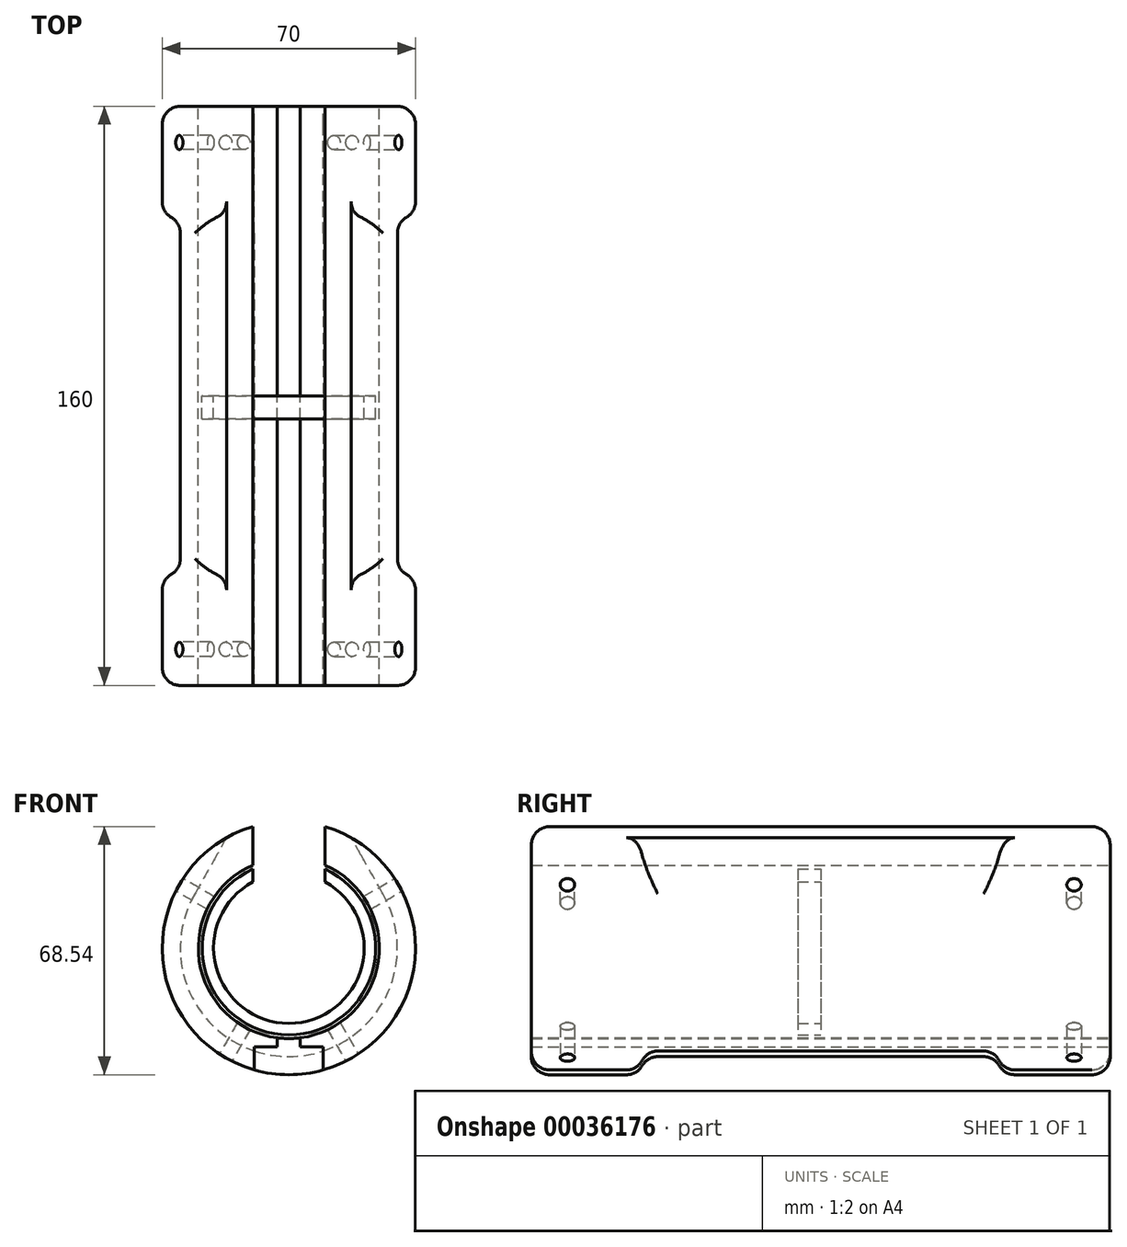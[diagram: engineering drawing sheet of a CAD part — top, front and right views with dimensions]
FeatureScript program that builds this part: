
annotation { "Feature Type Name" : "Feature", "Feature Type Description" : "" }
export const myFeature = defineFeature(function(context is Context, id is Id, definition is map)
    precondition{}
    {
        {
            assignVariable(context, id + "F0", {"name" : "Len", "anyValue" : 160 * mm});
        }
        {
            assignVariable(context, id + "F1", {"name" : "ScrewDia", "anyValue" : 4 * mm});
        }
        {
            assignVariable(context, id + "F2", {"name" : "FilletRadius", "anyValue" : 5 * mm});
        }
        {
            var Q0;
            Q0=qCreatedBy(makeId("Front.planeOp"),FACE);
            var sketch = newSketch(context, id + "F3", { "sketchPlane" : qUnion([Q0])});
            skArc(sketch, "E0", {"start": v(-10, 22.91) * mm, "mid": v(0, -25) * mm, "end": v(10, 22.91) * mm});
            skArc(sketch, "E1", {"start": v(-10, 33.54) * mm, "mid": v(0, -35) * mm, "end": v(10, 33.54) * mm});
            skPoint(sketch, "E2.orphan", {"position": v(-10, 33.54) * mm});
            skLineSegment(sketch, "E3", {"start": v(-10, 33.54) * mm, "end": v(-10, 22.91) * mm});
            skLineSegment(sketch, "E4", {"start": v(10, 33.54) * mm, "end": v(10, 22.91) * mm});
            skLineSegment(sketch, "E5", {"start": v(-17.5, -30.31) * mm, "end": v(17.5, -30.31) * mm, "construction": true});
            skLineSegment(sketch, "E6", {"start": v(17.5, -30.31) * mm, "end": v(30.31, 17.5) * mm, "construction": true});
            skLineSegment(sketch, "E7.MirrorCS", {"start": v(-17.5, -30.31) * mm, "end": v(-30.31, 17.5) * mm, "construction": true});
            skLineSegment(sketch, "E8", {"start": v(30.31, 17.5) * mm, "end": v(0, 0) * mm, "construction": true});
            skLineSegment(sketch, "E9", {"start": v(0, 0) * mm, "end": v(17.5, -30.31) * mm, "construction": true});
            skLineSegment(sketch, "E10", {"start": v(0, 0) * mm, "end": v(-17.5, -30.31) * mm, "construction": true});
            skLineSegment(sketch, "E11", {"start": v(0, 0) * mm, "end": v(-30.31, 17.5) * mm, "construction": true});
            skArc(sketch, "E12", {"start": v(-25.98, 15) * mm, "mid": v(0, -30) * mm, "end": v(25.98, 15) * mm});
            skLineSegment(sketch, "E13", {"start": v(-17.23, 30.46) * mm, "end": v(-25.98, 15) * mm});
            skLineSegment(sketch, "E14", {"start": v(-10, 22.91) * mm, "end": v(-17.23, 30.46) * mm, "construction": true});
            skLineSegment(sketch, "E15.MirrorCS", {"start": v(17.23, 30.46) * mm, "end": v(25.98, 15) * mm});
            skLineSegment(sketch, "E16.MirrorCS", {"start": v(10, 22.91) * mm, "end": v(17.23, 30.46) * mm, "construction": true});
            skLineSegment(sketch, "E17.left", {"start": v(-3.17, -24.8) * mm, "end": v(-3.17, -27.33) * mm});
            skLineSegment(sketch, "E17.right", {"start": v(3.18, -24.8) * mm, "end": v(3.18, -27.33) * mm});
            skLineSegment(sketch, "E18.top", {"start": v(9.53, -27.33) * mm, "end": v(3.18, -27.33) * mm});
            skLineSegment(sketch, "E18.left", {"start": v(9.53, -33.68) * mm, "end": v(9.53, -27.33) * mm});
            skLineSegment(sketch, "E18.right", {"start": v(-9.52, -33.68) * mm, "end": v(-9.52, -27.33) * mm});
            skLineSegment(sketch, "E19.trimOffspring", {"start": v(-3.17, -27.33) * mm, "end": v(-9.52, -27.33) * mm});
            skLineSegment(sketch, "E20", {"start": v(0, 0) * mm, "end": v(0, -25) * mm, "construction": true});
            skLineSegment(sketch, "E21", {"start": v(-21.65, 12.5) * mm, "end": v(-20.77, 12) * mm, "construction": true});
            skCircle(sketch, "E22", {"center": v(0, 0) * mm, "radius": 23.98 * mm, "construction": true});
            skLineSegment(sketch, "E23", {"start": v(-20.77, 12) * mm, "end": v(-18.02, 10.4) * mm, "construction": true});
            skArc(sketch, "E24", {"start": v(-10, 21.8) * mm, "mid": v(0, -23.98) * mm, "end": v(10, 21.8) * mm});
            skArc(sketch, "E25", {"start": v(-10, 18.25) * mm, "mid": v(0, -20.8) * mm, "end": v(10, 18.25) * mm});
            skLineSegment(sketch, "E26", {"start": v(-10, 21.8) * mm, "end": v(-10, 18.25) * mm});
            skLineSegment(sketch, "E27", {"start": v(10, 21.8) * mm, "end": v(10, 18.25) * mm});
            skLineSegment(sketch, "E28", {"start": v(0, 0) * mm, "end": v(-17.23, 30.46) * mm, "construction": true});
            skLineSegment(sketch, "E29", {"start": v(0, 0) * mm, "end": v(17.23, 30.46) * mm, "construction": true});
            skSolve(sketch);
        }
        {
            var Q0;
            {var subQ6=sQuery(id+"F3.wireOp",EDGE,"E4");Q0=makeQuery(id+"F3.imprint","IMPRINT",FACE,{"disambiguationData":[TD([[makeQuery(id+"F3.imprint","IMPRINT",EDGE,{"derivedFrom":subQ6}),1.0]])]});}
            var Q1;
            {var subQ4=sQuery(id+"F3.wireOp",EDGE,"E15.MirrorCS");Q1=makeQuery(id+"F3.imprint","IMPRINT",FACE,{"disambiguationData":[TD([[makeQuery(id+"F3.imprint","IMPRINT",EDGE,{"derivedFrom":subQ4}),1.0]])]});}
            var Q2;
            {var subQ3=sQuery(id+"F3.wireOp",EDGE,"E3");Q2=makeQuery(id+"F3.imprint","IMPRINT",FACE,{"disambiguationData":[TD([[makeQuery(id+"F3.imprint","IMPRINT",EDGE,{"derivedFrom":subQ3}),-1.0]])]});}
            var Q3;
            {var subQ5=sQuery(id+"F3.wireOp",EDGE,"E13");Q3=makeQuery(id+"F3.imprint","IMPRINT",FACE,{"disambiguationData":[TD([[makeQuery(id+"F3.imprint","IMPRINT",EDGE,{"derivedFrom":subQ5}),-1.0]])]});}
            extrude(context, id + "F4", {"entities" : qUnion([Q0, Q1, Q2, Q3]), "endBound" : BoundingType.SYMMETRIC, "depth" : getVariable(context, 'Len')});
        }
        {
            var Q0;
            {var subQ5=sQuery(id+"F3.wireOp",EDGE,"E18.left");Q0=makeQuery(id+"F3.imprint","IMPRINT",FACE,{"disambiguationData":[TD([[makeQuery(id+"F3.imprint","IMPRINT",EDGE,{"derivedFrom":subQ5}),1.0]])]});}
            var Q1;
            {var subQ6=sQuery(id+"F3.wireOp",EDGE,"E17.left");Q1=makeQuery(id+"F3.imprint","IMPRINT",FACE,{"disambiguationData":[TD([[makeQuery(id+"F3.imprint","IMPRINT",EDGE,{"derivedFrom":subQ6}),1.0]])]});}
            extrude(context, id + "F5", {"entities" : qUnion([Q0, Q1]), "endBound" : BoundingType.SYMMETRIC, "depth" : getVariable(context, 'Len')});
        }
        {
            var Q0;
            Q0=sQuery(id+"F3.wireOp",VERTEX,"E7.MirrorCS.start");
            var Q1;
            Q1=sQuery(id+"F3.wireOp",EDGE,"E10");
            cPlane(context, id + "F6", {"entities" : qUnion([Q0, Q1]), "cplaneType" : CPlaneType.LINE_POINT, "offset" : 152.4 * mm, "width" : 152.4 * mm, "height" : 152.4 * mm});
        }
        {
            var Q0;
            Q0=qCreatedBy(id+"F6.planeOp",FACE);
            var sketch = newSketch(context, id + "F7", { "sketchPlane" : qUnion([Q0])});
            skPoint(sketch, "E30", {"position": v(0, 70) * mm});
            skPoint(sketch, "E31", {"position": v(0, -70) * mm});
            skSolve(sketch);
        }
        {
            var Q0;
            Q0=sQuery(id+"F3.wireOp",VERTEX,"E6.start");
            var Q1;
            Q1=sQuery(id+"F3.wireOp",EDGE,"E9");
            cPlane(context, id + "F8", {"entities" : qUnion([Q0, Q1]), "cplaneType" : CPlaneType.LINE_POINT, "offset" : 152.4 * mm, "width" : 152.4 * mm, "height" : 152.4 * mm});
        }
        {
            var Q0;
            Q0=qCreatedBy(id+"F8.planeOp",FACE);
            var sketch = newSketch(context, id + "F9", { "sketchPlane" : qUnion([Q0])});
            skPoint(sketch, "E32", {"position": v(0, 70) * mm});
            skPoint(sketch, "E33", {"position": v(0, -70) * mm});
            skSolve(sketch);
        }
        {
            var Q0;
            Q0=sQuery(id+"F3.wireOp",EDGE,"E8");
            var Q1;
            Q1=sQuery(id+"F3.wireOp",VERTEX,"E6.end");
            cPlane(context, id + "F10", {"entities" : qUnion([Q0, Q1]), "cplaneType" : CPlaneType.LINE_POINT, "offset" : 152.4 * mm, "width" : 152.4 * mm, "height" : 152.4 * mm});
        }
        {
            var Q0;
            Q0=qCreatedBy(id+"F10.planeOp",FACE);
            var sketch = newSketch(context, id + "F11", { "sketchPlane" : qUnion([Q0])});
            skPoint(sketch, "E34", {"position": v(70, 0) * mm});
            skPoint(sketch, "E35", {"position": v(-70, 0) * mm});
            skSolve(sketch);
        }
        {
            var Q0;
            Q0=sQuery(id+"F3.wireOp",VERTEX,"E7.MirrorCS.end");
            var Q1;
            Q1=sQuery(id+"F3.wireOp",EDGE,"E11");
            cPlane(context, id + "F12", {"entities" : qUnion([Q0, Q1]), "cplaneType" : CPlaneType.LINE_POINT, "offset" : 152.4 * mm, "width" : 152.4 * mm, "height" : 152.4 * mm});
        }
        {
            var Q0;
            Q0=qCreatedBy(id+"F12.planeOp",FACE);
            var sketch = newSketch(context, id + "F13", { "sketchPlane" : qUnion([Q0])});
            skPoint(sketch, "E36", {"position": v(70, 0) * mm});
            skPoint(sketch, "E37", {"position": v(-70, 0) * mm});
            skSolve(sketch);
        }
        {
            var Q0;
            Q0=sQuery(id+"F13.wireOp",VERTEX,"E36");
            var Q1;
            Q1=sQuery(id+"F7.wireOp",VERTEX,"E30");
            var Q2;
            Q2=sQuery(id+"F9.wireOp",VERTEX,"E32");
            var Q3;
            Q3=sQuery(id+"F13.wireOp",VERTEX,"E37");
            var Q4;
            Q4=sQuery(id+"F7.wireOp",VERTEX,"E31");
            var Q5;
            Q5=sQuery(id+"F9.wireOp",VERTEX,"E33");
            var Q6;
            Q6=makeQuery(id+"F4.opExtrude","SWEPT_BODY",BODY,{"disambiguationData":[OSD([sQuery(id+"F3.wireOp",EDGE,"E0"),sQuery(id+"F3.wireOp",EDGE,"E1"),sQuery(id+"F3.wireOp",EDGE,"E3"),sQuery(id+"F3.wireOp",EDGE,"E17.left"),sQuery(id+"F3.wireOp",EDGE,"E18.right"),sQuery(id+"F3.wireOp",EDGE,"E19.trimOffspring")])]});
            var Q7;
            Q7=makeQuery(id+"F4.opExtrude","SWEPT_BODY",BODY,{"disambiguationData":[OSD([sQuery(id+"F3.wireOp",EDGE,"E0"),sQuery(id+"F3.wireOp",EDGE,"E1"),sQuery(id+"F3.wireOp",EDGE,"E4"),sQuery(id+"F3.wireOp",EDGE,"E17.right"),sQuery(id+"F3.wireOp",EDGE,"E18.top"),sQuery(id+"F3.wireOp",EDGE,"E18.left")])]});
            hole(context, id + "F14", {"style" : HoleStyle.SIMPLE, "holeDiameter" : getVariable(context, 'ScrewDia'), "endStyle" : HoleEndStyle.BLIND, "holeDepth" : 12.7 * mm, "locations" : qUnion([Q0, Q1, Q2, Q3, Q4, Q5]), "scope" : qUnion([Q6, Q7])});
        }
        {
            var Q0;
            Q0=makeQuery(id+"F3.imprint","IMPRINT",FACE,{"disambiguationData":[TD([[makeQuery(id+"F3.imprint","IMPRINT",EDGE,{"derivedFrom":sQuery(id+"F3.wireOp",EDGE,"E12")}),-1.0]])]});
            var Q1;
            {var subQ5=sQuery(id+"F3.wireOp",EDGE,"E18.left");Q1=makeQuery(id+"F3.imprint","IMPRINT",FACE,{"disambiguationData":[TD([[makeQuery(id+"F3.imprint","IMPRINT",EDGE,{"derivedFrom":subQ5}),1.0]])]});}
            extrude(context, id + "F15", {"entities" : qUnion([Q0, Q1]), "operationType" : NewBodyOperationType.REMOVE, "endBound" : BoundingType.SYMMETRIC, "oppositeDirection" : true, "depth" : 100 * mm});
        }
        {
            var Q0;
            Q0=makeQuery(id+"F4.opExtrude","CAP_EDGE",EDGE,{"disambiguationData":[OSD([sQuery(id+"F3.wireOp",EDGE,"E1")])],"isStart":false});
            var Q1;
            Q1=makeQuery(id+"F4.opExtrude","CAP_EDGE",EDGE,{"disambiguationData":[OSD([sQuery(id+"F3.wireOp",EDGE,"E1")])],"isStart":true});
            var Q2;
            Q2=makeQuery(id+"F15.boolean.opBoolean","COPY",EDGE,{"derivedFrom":makeQuery(id+"F15.opExtrude","CAP_EDGE",EDGE,{"disambiguationData":[OSD([sQuery(id+"F3.wireOp",EDGE,"E12")])],"isStart":true})});
            var Q3;
            Q3=makeQuery(id+"F15.boolean.opBoolean","COPY",EDGE,{"derivedFrom":makeQuery(id+"F15.opExtrude","CAP_EDGE",EDGE,{"disambiguationData":[OSD([sQuery(id+"F3.wireOp",EDGE,"E12")])],"isStart":false})});
            var Q4;
            Q4=makeQuery(id+"F5.opExtrude","CAP_EDGE",EDGE,{"disambiguationData":[OSD([sQuery(id+"F3.wireOp",EDGE,"E1")])],"isStart":true});
            var Q5;
            Q5=makeQuery(id+"F5.opExtrude","CAP_EDGE",EDGE,{"disambiguationData":[OSD([sQuery(id+"F3.wireOp",EDGE,"E1")])],"isStart":false});
            fillet(context, id + "F16", {"entities" : qUnion([Q0, Q1, Q2, Q3, Q4, Q5]), "radius" : getVariable(context, 'FilletRadius'), "tangentPropagation" : true, "allowEdgeOverflow" : false});
        }
        {
            var Q0;
            Q0=makeQuery(id+"F16.opFillet","BLEND_EDGE",EDGE,{"blendedFrom":[makeQuery(id+"F15.boolean.opBoolean","COPY",EDGE,{"derivedFrom":makeQuery(id+"F15.opExtrude","CAP_EDGE",EDGE,{"disambiguationData":[OSD([sQuery(id+"F3.wireOp",EDGE,"E13")])],"isStart":false})}),makeQuery(id+"F4.opExtrude","SWEPT_FACE",FACE,{"disambiguationData":[OSD([sQuery(id+"F3.wireOp",EDGE,"E1")])]})],"blendedInto":[makeQuery(id+"F4.opExtrude","SWEPT_FACE",FACE,{"disambiguationData":[OSD([sQuery(id+"F3.wireOp",EDGE,"E1")])]})]});
            var Q1;
            {var subQ0=sQuery(id+"F3.wireOp",EDGE,"E12");var subQ1=sQuery(id+"F3.wireOp",EDGE,"E1");Q1=makeQuery(id+"F16.opFillet","BLEND_EDGE",EDGE,{"blendedFrom":[makeQuery(id+"F15.boolean.opBoolean","COPY",EDGE,{"disambiguationData":[OD(2.0)],"derivedFrom":makeQuery(id+"F15.opExtrude","CAP_EDGE",EDGE,{"disambiguationData":[OSD([subQ0])],"isStart":false})}),makeQuery(id+"F15.boolean.opBoolean","SPLIT",FACE,{"disambiguationData":[TD([makeQuery(id+"F15.opExtrude","CAP_FACE",FACE,{"disambiguationData":[OSD([subQ1,subQ0,sQuery(id+"F3.wireOp",EDGE,"E13"),sQuery(id+"F3.wireOp",EDGE,"E15.MirrorCS")])],"isStart":false})])],"derivedFrom":makeQuery(id+"F5.opExtrude","SWEPT_FACE",FACE,{"disambiguationData":[OSD([subQ1])]})})],"blendedInto":[makeQuery(id+"F15.boolean.opBoolean","SPLIT",FACE,{"disambiguationData":[TD([makeQuery(id+"F15.opExtrude","CAP_FACE",FACE,{"disambiguationData":[OSD([subQ1,subQ0,sQuery(id+"F3.wireOp",EDGE,"E13"),sQuery(id+"F3.wireOp",EDGE,"E15.MirrorCS")])],"isStart":false})])],"derivedFrom":makeQuery(id+"F5.opExtrude","SWEPT_FACE",FACE,{"disambiguationData":[OSD([subQ1])]})})]});}
            var Q2;
            {var subQ0=sQuery(id+"F3.wireOp",EDGE,"E1");var subQ1=makeQuery(id+"F3.imprint","INTERSECT",VERTEX,{"derivedFrom":[subQ0,sQuery(id+"F3.wireOp",EDGE,"E15.MirrorCS")]});Q2=makeQuery(id+"F16.opFillet","BLEND_EDGE",EDGE,{"blendedFrom":[makeQuery(id+"F15.boolean.opBoolean","COPY",EDGE,{"disambiguationData":[OD(1.0)],"derivedFrom":makeQuery(id+"F15.opExtrude","CAP_EDGE",EDGE,{"disambiguationData":[OSD([sQuery(id+"F3.wireOp",EDGE,"E12")])],"isStart":false})}),makeQuery(id+"F4.opExtrude","SWEPT_FACE",FACE,{"disambiguationData":[OSD([subQ0]),TDD([makeQuery(id+"F3.imprint","IMPRINT",EDGE,{"disambiguationData":[TD([[subQ1,1.0]])],"derivedFrom":subQ0}),makeQuery(id+"F3.imprint","IMPRINT",EDGE,{"disambiguationData":[TD([[makeQuery(id+"F3.imprint","INTERSECT",VERTEX,{"derivedFrom":[subQ0,sQuery(id+"F3.wireOp",EDGE,"E4")]}),1.0]])],"derivedFrom":subQ0})])]})],"blendedInto":[makeQuery(id+"F4.opExtrude","SWEPT_FACE",FACE,{"disambiguationData":[OSD([subQ0]),TDD([makeQuery(id+"F3.imprint","IMPRINT",EDGE,{"disambiguationData":[TD([[subQ1,1.0]])],"derivedFrom":subQ0}),makeQuery(id+"F3.imprint","IMPRINT",EDGE,{"disambiguationData":[TD([[makeQuery(id+"F3.imprint","INTERSECT",VERTEX,{"derivedFrom":[subQ0,sQuery(id+"F3.wireOp",EDGE,"E4")]}),1.0]])],"derivedFrom":subQ0})])]})]});}
            var Q3;
            {var subQ0=sQuery(id+"F3.wireOp",EDGE,"E12");var subQ1=sQuery(id+"F3.wireOp",EDGE,"E1");Q3=makeQuery(id+"F16.opFillet","BLEND_EDGE",EDGE,{"blendedFrom":[makeQuery(id+"F15.boolean.opBoolean","COPY",EDGE,{"disambiguationData":[OD(2.0)],"derivedFrom":makeQuery(id+"F15.opExtrude","CAP_EDGE",EDGE,{"disambiguationData":[OSD([subQ0])],"isStart":true})}),makeQuery(id+"F15.boolean.opBoolean","SPLIT",FACE,{"disambiguationData":[TD([makeQuery(id+"F15.opExtrude","CAP_FACE",FACE,{"disambiguationData":[OSD([subQ1,subQ0,sQuery(id+"F3.wireOp",EDGE,"E13"),sQuery(id+"F3.wireOp",EDGE,"E15.MirrorCS")])],"isStart":true})])],"derivedFrom":makeQuery(id+"F5.opExtrude","SWEPT_FACE",FACE,{"disambiguationData":[OSD([subQ1])]})})],"blendedInto":[makeQuery(id+"F15.boolean.opBoolean","SPLIT",FACE,{"disambiguationData":[TD([makeQuery(id+"F15.opExtrude","CAP_FACE",FACE,{"disambiguationData":[OSD([subQ1,subQ0,sQuery(id+"F3.wireOp",EDGE,"E13"),sQuery(id+"F3.wireOp",EDGE,"E15.MirrorCS")])],"isStart":true})])],"derivedFrom":makeQuery(id+"F5.opExtrude","SWEPT_FACE",FACE,{"disambiguationData":[OSD([subQ1])]})})]});}
            var Q4;
            {var subQ0=sQuery(id+"F3.wireOp",EDGE,"E13");var subQ1=sQuery(id+"F3.wireOp",EDGE,"E1");var subQ2=makeQuery(id+"F3.imprint","INTERSECT",VERTEX,{"derivedFrom":[subQ1,subQ0]});var subQ3=sQuery(id+"F3.wireOp",EDGE,"E18.right");var subQ4=sQuery(id+"F3.wireOp",EDGE,"E12");Q4=makeQuery(id+"F16.opFillet","BLEND_EDGE",EDGE,{"blendedFrom":[makeQuery(id+"F15.boolean.opBoolean","COPY",EDGE,{"disambiguationData":[TD([makeQuery(id+"F4.opExtrude","SWEPT_FACE",FACE,{"disambiguationData":[OSD([subQ3])]})])],"derivedFrom":makeQuery(id+"F15.opExtrude","CAP_EDGE",EDGE,{"disambiguationData":[OSD([subQ4])],"isStart":false})}),makeQuery(id+"F4.opExtrude","SWEPT_FACE",FACE,{"disambiguationData":[OSD([subQ1]),TDD([makeQuery(id+"F3.imprint","IMPRINT",EDGE,{"disambiguationData":[TD([[makeQuery(id+"F3.imprint","INTERSECT",VERTEX,{"derivedFrom":[subQ1,sQuery(id+"F3.wireOp",EDGE,"E3")]}),-1.0]])],"derivedFrom":subQ1}),makeQuery(id+"F3.imprint","IMPRINT",EDGE,{"disambiguationData":[TD([[subQ2,-1.0]])],"derivedFrom":subQ1})])]})],"blendedInto":[makeQuery(id+"F4.opExtrude","SWEPT_FACE",FACE,{"disambiguationData":[OSD([subQ1]),TDD([makeQuery(id+"F3.imprint","IMPRINT",EDGE,{"disambiguationData":[TD([[makeQuery(id+"F3.imprint","INTERSECT",VERTEX,{"derivedFrom":[subQ1,sQuery(id+"F3.wireOp",EDGE,"E3")]}),-1.0]])],"derivedFrom":subQ1}),makeQuery(id+"F3.imprint","IMPRINT",EDGE,{"disambiguationData":[TD([[subQ2,-1.0]])],"derivedFrom":subQ1})])]})]});}
            var Q5;
            {var subQ0=sQuery(id+"F3.wireOp",EDGE,"E1");var subQ1=sQuery(id+"F3.wireOp",EDGE,"E15.MirrorCS");var subQ2=makeQuery(id+"F3.imprint","INTERSECT",VERTEX,{"derivedFrom":[subQ0,subQ1]});var subQ3=sQuery(id+"F3.wireOp",EDGE,"E18.left");var subQ4=sQuery(id+"F3.wireOp",EDGE,"E12");Q5=makeQuery(id+"F16.opFillet","BLEND_EDGE",EDGE,{"blendedFrom":[makeQuery(id+"F15.boolean.opBoolean","COPY",EDGE,{"disambiguationData":[TD([makeQuery(id+"F4.opExtrude","SWEPT_FACE",FACE,{"disambiguationData":[OSD([subQ3])]})])],"derivedFrom":makeQuery(id+"F15.opExtrude","CAP_EDGE",EDGE,{"disambiguationData":[OSD([subQ4])],"isStart":true})}),makeQuery(id+"F4.opExtrude","SWEPT_FACE",FACE,{"disambiguationData":[OSD([subQ0]),TDD([makeQuery(id+"F3.imprint","IMPRINT",EDGE,{"disambiguationData":[TD([[subQ2,1.0]])],"derivedFrom":subQ0}),makeQuery(id+"F3.imprint","IMPRINT",EDGE,{"disambiguationData":[TD([[makeQuery(id+"F3.imprint","INTERSECT",VERTEX,{"derivedFrom":[subQ0,sQuery(id+"F3.wireOp",EDGE,"E4")]}),1.0]])],"derivedFrom":subQ0})])]})],"blendedInto":[makeQuery(id+"F4.opExtrude","SWEPT_FACE",FACE,{"disambiguationData":[OSD([subQ0]),TDD([makeQuery(id+"F3.imprint","IMPRINT",EDGE,{"disambiguationData":[TD([[subQ2,1.0]])],"derivedFrom":subQ0}),makeQuery(id+"F3.imprint","IMPRINT",EDGE,{"disambiguationData":[TD([[makeQuery(id+"F3.imprint","INTERSECT",VERTEX,{"derivedFrom":[subQ0,sQuery(id+"F3.wireOp",EDGE,"E4")]}),1.0]])],"derivedFrom":subQ0})])]})]});}
            var Q6;
            {var subQ0=sQuery(id+"F3.wireOp",EDGE,"E13");var subQ1=sQuery(id+"F3.wireOp",EDGE,"E1");var subQ2=makeQuery(id+"F3.imprint","INTERSECT",VERTEX,{"derivedFrom":[subQ1,subQ0]});var subQ3=sQuery(id+"F3.wireOp",EDGE,"E18.right");var subQ4=sQuery(id+"F3.wireOp",EDGE,"E12");Q6=makeQuery(id+"F16.opFillet","BLEND_EDGE",EDGE,{"blendedFrom":[makeQuery(id+"F15.boolean.opBoolean","COPY",EDGE,{"disambiguationData":[TD([makeQuery(id+"F4.opExtrude","SWEPT_FACE",FACE,{"disambiguationData":[OSD([subQ3])]})])],"derivedFrom":makeQuery(id+"F15.opExtrude","CAP_EDGE",EDGE,{"disambiguationData":[OSD([subQ4])],"isStart":true})}),makeQuery(id+"F4.opExtrude","SWEPT_FACE",FACE,{"disambiguationData":[OSD([subQ1]),TDD([makeQuery(id+"F3.imprint","IMPRINT",EDGE,{"disambiguationData":[TD([[makeQuery(id+"F3.imprint","INTERSECT",VERTEX,{"derivedFrom":[subQ1,sQuery(id+"F3.wireOp",EDGE,"E3")]}),-1.0]])],"derivedFrom":subQ1}),makeQuery(id+"F3.imprint","IMPRINT",EDGE,{"disambiguationData":[TD([[subQ2,-1.0]])],"derivedFrom":subQ1})])]})],"blendedInto":[makeQuery(id+"F4.opExtrude","SWEPT_FACE",FACE,{"disambiguationData":[OSD([subQ1]),TDD([makeQuery(id+"F3.imprint","IMPRINT",EDGE,{"disambiguationData":[TD([[makeQuery(id+"F3.imprint","INTERSECT",VERTEX,{"derivedFrom":[subQ1,sQuery(id+"F3.wireOp",EDGE,"E3")]}),-1.0]])],"derivedFrom":subQ1}),makeQuery(id+"F3.imprint","IMPRINT",EDGE,{"disambiguationData":[TD([[subQ2,-1.0]])],"derivedFrom":subQ1})])]})]});}
            fillet(context, id + "F17", {"entities" : qUnion([Q0, Q1, Q2, Q3, Q4, Q5, Q6]), "radius" : getVariable(context, 'FilletRadius'), "tangentPropagation" : true, "allowEdgeOverflow" : false});
        }
        {
            var Q0;
            Q0=sQuery(id+"F11.wireOp",VERTEX,"E34");
            var Q1;
            Q1=sQuery(id+"F11.wireOp",VERTEX,"E35");
            var Q2;
            Q2=makeQuery(id+"F4.opExtrude","SWEPT_BODY",BODY,{"disambiguationData":[OSD([sQuery(id+"F3.wireOp",EDGE,"E0"),sQuery(id+"F3.wireOp",EDGE,"E1"),sQuery(id+"F3.wireOp",EDGE,"E4"),sQuery(id+"F3.wireOp",EDGE,"E17.right"),sQuery(id+"F3.wireOp",EDGE,"E18.top"),sQuery(id+"F3.wireOp",EDGE,"E18.left")])]});
            hole(context, id + "F18", {"style" : HoleStyle.SIMPLE, "holeDiameter" : getVariable(context, 'ScrewDia'), "endStyle" : HoleEndStyle.BLIND, "oppositeDirection" : true, "holeDepth" : 12.7 * mm, "locations" : qUnion([Q0, Q1]), "scope" : qUnion([Q2])});
        }
        {
            var Q0;
            Q0=makeQuery(id+"F3.imprint","IMPRINT",FACE,{"disambiguationData":[TD([[makeQuery(id+"F3.imprint","IMPRINT",EDGE,{"derivedFrom":sQuery(id+"F3.wireOp",EDGE,"E24")}),1.0]])]});
            extrude(context, id + "F19", {"entities" : qUnion([Q0]), "depth" : 6.35 * mm});
        }
    });
